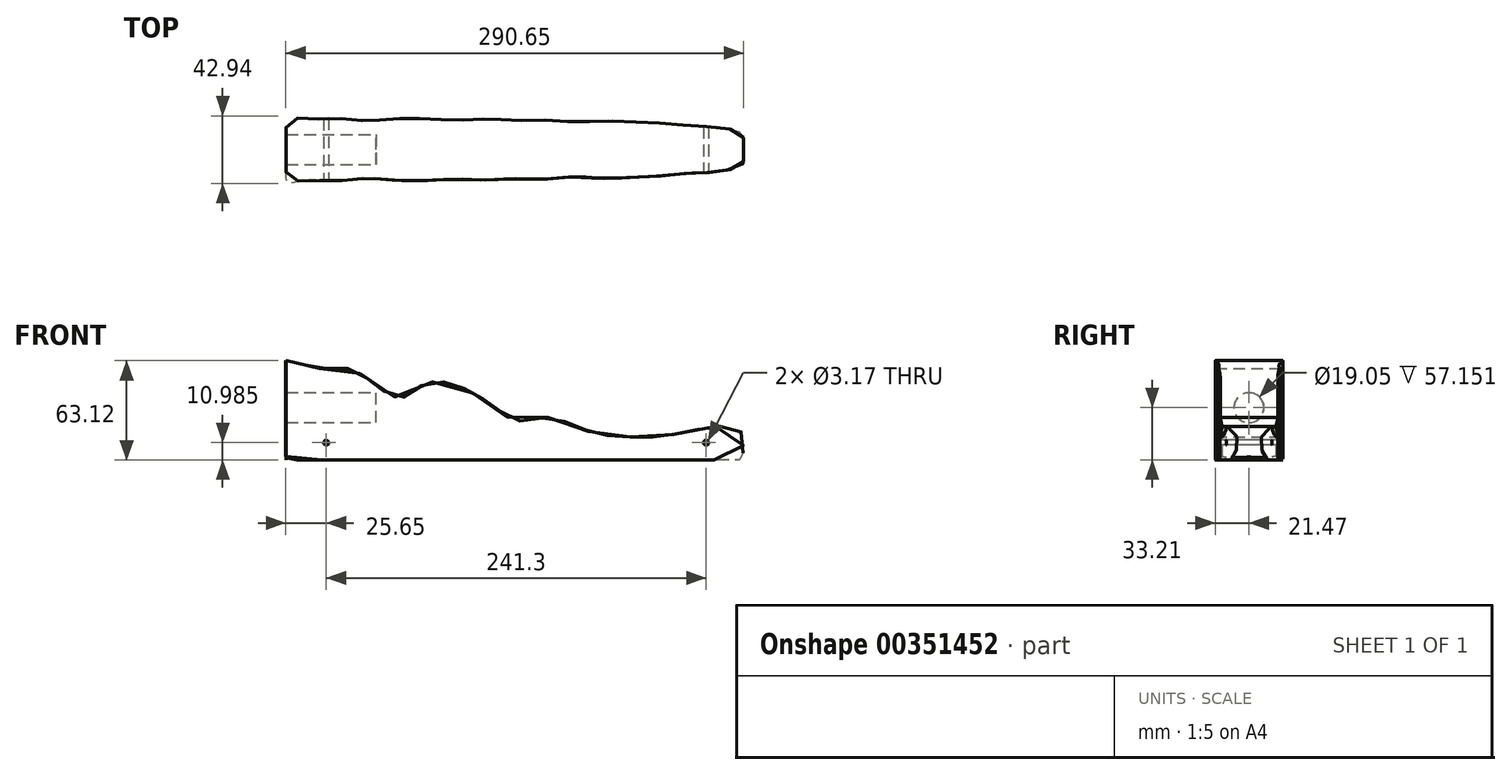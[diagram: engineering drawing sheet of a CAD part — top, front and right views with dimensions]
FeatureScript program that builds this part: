
annotation { "Feature Type Name" : "Feature", "Feature Type Description" : "" }
export const myFeature = defineFeature(function(context is Context, id is Id, definition is map)
    precondition{}
    {
        {
            var Q0;
            Q0=qCreatedBy(makeId("Front.planeOp"),FACE);
            var sketch = newSketch(context, id + "F0", { "sketchPlane" : qUnion([Q0])});
            skLineSegment(sketch, "E0.bottom", {"start": v(-147.08, 25.02) * mm, "end": v(145.02, 25.02) * mm, "construction": true});
            skLineSegment(sketch, "E0.top", {"start": v(-146.05, -38.48) * mm, "end": v(145.02, -38.48) * mm, "construction": true});
            skLineSegment(sketch, "E0.left", {"start": v(-147.08, 25.02) * mm, "end": v(-147.08, -34.54) * mm, "construction": true});
            skLineSegment(sketch, "E0.right", {"start": v(145.02, 25.02) * mm, "end": v(145.02, -38.48) * mm, "construction": true});
            skFitSpline(sketch, "E1", {"points": [v(-145.6, -31.9) * mm, v(-147.72, -19.6) * mm, v(-147.79, 26.92) * mm, v(-147.99, 29.34) * mm, v(-142.02, 29.61) * mm, v(-125.05, 25.02) * mm, v(-102.83, 23.6) * mm, v(-74.46, 6.24) * mm, v(-54.2, 16.24) * mm, v(-12.91, 0) * mm, v(0, -8.53) * mm, v(21.42, -6.4) * mm, v(47.36, -15.45) * mm, v(74.76, -18.6) * mm, v(98.36, -17.29) * mm, v(127.68, -11.92) * mm, v(136.76, -12.9) * mm, v(143.1, -15.6) * mm, v(144.35, -21) * mm, v(143.3, -32.27) * mm, v(141.14, -33.07) * mm, v(120.6, -33.2) * mm, v(104.27, -33.2) * mm, v(82.72, -33.2) * mm, v(63.7, -33.2) * mm, v(51.28, -33.2) * mm, v(25.47, -33.2) * mm, v(9.56, -33.2) * mm, v(-16.64, -33.2) * mm, v(-51.21, -33.2) * mm, v(-71.53, -33.2) * mm, v(-93.55, -33.19) * mm, v(-109.29, -33.19) * mm, v(-123.97, -33.19) * mm, v(-139.1, -33.13) * mm, v(-145.6, -31.9) * mm]});
            skSolve(sketch);
        }
        {
            var Q0;
            Q0=qCreatedBy(makeId("Top.planeOp"),FACE);
            var sketch = newSketch(context, id + "F1", { "sketchPlane" : qUnion([Q0])});
            skLineSegment(sketch, "E2.bottom", {"start": v(-146.05, 22.22) * mm, "end": v(146.05, 22.23) * mm, "construction": true});
            skLineSegment(sketch, "E2.top", {"start": v(-146.05, -22.23) * mm, "end": v(146.05, -22.22) * mm, "construction": true});
            skLineSegment(sketch, "E2.left", {"start": v(-146.05, 22.23) * mm, "end": v(-146.05, -22.23) * mm, "construction": true});
            skLineSegment(sketch, "E2.right", {"start": v(146.05, 22.43) * mm, "end": v(146.05, -22.22) * mm, "construction": true});
            skLineSegment(sketch, "E3", {"start": v(-146.05, 0) * mm, "end": v(146.05, 0.1) * mm, "construction": true});
            skFitSpline(sketch, "E4", {"points": [v(-146.05, 0) * mm, v(-146.14, 12.26) * mm, v(-145.25, 21.17) * mm, v(-137.17, 19.55) * mm, v(-116.42, 20.02) * mm, v(-95.33, 18.26) * mm, v(-79.6, 19.34) * mm, v(-55.8, 19.54) * mm, v(-34.63, 18.85) * mm, v(-19.18, 19.54) * mm, v(-2.75, 18.6) * mm, v(10.78, 18.83) * mm, v(31.06, 17.88) * mm, v(40.04, 17.2) * mm, v(51.69, 18.35) * mm, v(70.04, 17.88) * mm, v(83.12, 17.4) * mm, v(93.58, 16.7) * mm, v(103.56, 15.75) * mm, v(116.18, 14.8) * mm, v(127.6, 14.3) * mm, v(136.17, 12.87) * mm, v(142.24, 10.93) * mm, v(146.05, 0.1) * mm], "startDerivative": vector(0, 335.54) * mm, "endDerivative": vector(0, -277.49) * mm});
            skFitSpline(sketch, "E5.MirrorCS", {"points": [v(-146.05, 0) * mm, v(-146.13, -12.26) * mm, v(-145.23, -21.17) * mm, v(-137.15, -19.54) * mm, v(-116.4, -20) * mm, v(-95.31, -18.22) * mm, v(-79.6, -19.3) * mm, v(-55.8, -19.48) * mm, v(-34.61, -18.77) * mm, v(-19.17, -19.45) * mm, v(-2.74, -18.5) * mm, v(10.8, -18.72) * mm, v(31.07, -17.75) * mm, v(40.05, -17.06) * mm, v(51.7, -18.2) * mm, v(70.06, -17.73) * mm, v(83.13, -17.24) * mm, v(93.6, -16.52) * mm, v(103.57, -15.57) * mm, v(116.2, -14.61) * mm, v(127.62, -14.1) * mm, v(136.18, -12.67) * mm, v(142.25, -10.72) * mm, v(146.05, 0.1) * mm], "startDerivative": vector(0.24, -335.54) * mm, "endDerivative": vector(-0.2, 277.49) * mm});
            skLineSegment(sketch, "E6.MirrorCS", {"start": v(-146.03, -22.22) * mm, "end": v(146.07, -22.02) * mm});
            skSolve(sketch);
        }
        {
            var Q0;
            Q0=qCreatedBy(makeId("Right.planeOp"),FACE);
            var sketch = newSketch(context, id + "F2", { "sketchPlane" : qUnion([Q0])});
            skCircle(sketch, "E7", {"center": v(0, 0) * mm, "radius": 9.53 * mm});
            skSolve(sketch);
        }
        {
            var Q0;
            Q0=qCreatedBy(makeId("Front.planeOp"),FACE);
            var sketch = newSketch(context, id + "F3", { "sketchPlane" : qUnion([Q0])});
            skCircle(sketch, "E8", {"center": v(-120.65, -22.22) * mm, "radius": 1.59 * mm});
            skCircle(sketch, "E9", {"center": v(120.65, -22.23) * mm, "radius": 1.59 * mm});
            skSolve(sketch);
        }
        {
            var Q0;
            Q0=qSketchRegion(id+"F0",true);
            extrude(context, id + "F4", {"entities" : qUnion([Q0]), "depth" : 44.45 * mm, "symmetric" : true});
        }
        {
            var Q0;
            Q0=makeQuery(id+"F1.imprint","IMPRINT",FACE,{"disambiguationData":[TD([[makeQuery(id+"F1.imprint","IMPRINT",EDGE,{"derivedFrom":sQuery(id+"F1.wireOp",EDGE,"E4")}),-1.0]])]});
            var Q1;
            Q1=sQuery(id+"F1.wireOp",EDGE,"E5.MirrorCS");
            var Q2;
            Q2=sQuery(id+"F1.wireOp",EDGE,"E4");
            extrude(context, id + "F5", {"entities" : qUnion([Q0]), "operationType" : NewBodyOperationType.INTERSECT, "surfaceEntities" : qUnion([Q1, Q2]), "endBound" : BoundingType.THROUGH_ALL, "oppositeDirection" : true, "depth" : 63.5 * mm, "hasSecondDirection" : true, "secondDirectionBound" : BoundingType.THROUGH_ALL, "secondDirectionOppositeDirection" : false, "secondDirectionDepth" : 25.4 * mm});
        }
        {
            var Q0;
            Q0=qSketchRegion(id+"F2",true);
            extrude(context, id + "F6", {"entities" : qUnion([Q0]), "operationType" : NewBodyOperationType.REMOVE, "oppositeDirection" : true, "depth" : 152.4 * mm, "hasSecondDirection" : true, "secondDirectionOppositeDirection" : true, "secondDirectionDepth" : 88.9 * mm});
        }
        {
            var Q0;
            Q0=qSketchRegion(id+"F3",true);
            extrude(context, id + "F7", {"entities" : qUnion([Q0]), "operationType" : NewBodyOperationType.REMOVE, "oppositeDirection" : true, "depth" : 50.8 * mm, "symmetric" : true});
        }
    });
